# Revit family: Enna Desk - ETL
name_source: partatom
category: Lighting Fixtures
revit_build: Autodesk Revit 2018 (Build: 20170223_1515(x64)
units: mm (PartAtom-declared; Revit-internal decimal feet)

## family parameters
Always vertical = Yes
Cut with Voids When Loaded = No
Light Source = No
OmniClass Number = 23.80.70.00
OmniClass Title = Lighting
Part Type = Normal
Room Calculation Point = No
Round Connector Dimension = Use Diameter
Shared = No
Work Plane-Based = No

## types (3) — shared parameters
Colour Temperature = 2700K
Lamp = LED
Manufacturer = Astro
Product Load (Watts) = 4
Switched = Yes

## per-type parameters (varying)
| type | Legacy Code | Product Name | SKU Code |
| Enna Desk - White | 8341 | Enna Desk LED - Matt White | 1058092 |
| Enna Desk - Black | 8342 | Enna Desk LED - Matt Black | 1058093 |
| Enna Desk - Matt Gold | 8343 | Enna Desk LED - Matt Gold | 1058094 |

## geometry (parser evidence)
native form markers: Sweep x2
no freeform markers — native parametric forms only
